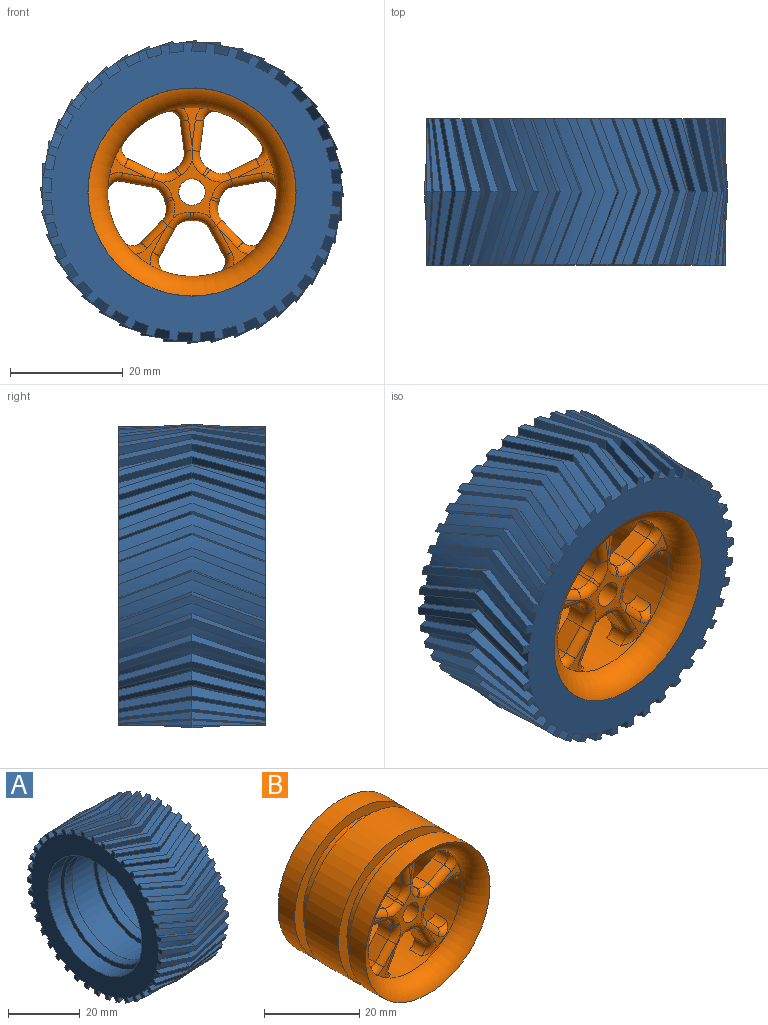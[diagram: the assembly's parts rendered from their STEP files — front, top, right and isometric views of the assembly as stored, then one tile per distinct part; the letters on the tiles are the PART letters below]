
ASSEMBLY  parts=2 mates=1
PART A: 251 faces, bbox 26x53.9x53.9 mm
  f0: cylinder r=25mm len=26mm, axis (-1,0,0), area 62.9mm2, adj f49,f50,f243,f244,f246,f247
  f1: cylinder r=25mm len=26mm, axis (-1,0,0), area 62.9mm2, adj f49,f50,f51,f52,f248,f249
  f2: cylinder r=25mm len=26mm, axis (-1,0,0), area 62.9mm2, adj f49,f50,f238,f239,f241,f242
  f3: cylinder r=25mm len=26mm, axis (-1,0,0), area 62.9mm2, adj f49,f50,f233,f234,f236,f237
  f4: cylinder r=25mm len=26mm, axis (-1,0,0), area 62.9mm2, adj f49,f50,f228,f229,f231,f232
  f5: cylinder r=25mm len=26mm, axis (-1,0,0), area 62.9mm2, adj f49,f50,f223,f224,f226,f227
  f6: cylinder r=25mm len=26mm, axis (-1,0,0), area 62.9mm2, adj f49,f50,f218,f219,f221,f222
  f7: cylinder r=25mm len=26mm, axis (-1,0,0), area 62.9mm2, adj f49,f50,f213,f214,f216,f217
  f8: cylinder r=25mm len=26mm, axis (-1,0,0), area 62.9mm2, adj f49,f50,f208,f209,f211,f212
  f9: cylinder r=25mm len=26mm, axis (-1,0,0), area 62.9mm2, adj f49,f50,f203,f204,f206,f207
  f10: cylinder r=25mm len=26mm, axis (-1,0,0), area 62.9mm2, adj f49,f50,f198,f199,f201,f202
  f11: cylinder r=25mm len=26mm, axis (-1,0,0), area 62.9mm2, adj f49,f50,f193,f194,f196,f197
  f12: cylinder r=25mm len=26mm, axis (-1,0,0), area 62.9mm2, adj f49,f50,f188,f189,f191,f192
  f13: cylinder r=25mm len=26mm, axis (-1,0,0), area 62.9mm2, adj f49,f50,f183,f184,f186,f187
  f14: cylinder r=25mm len=26mm, axis (-1,0,0), area 62.9mm2, adj f49,f50,f178,f179,f181,f182
  f15: cylinder r=25mm len=26mm, axis (-1,0,0), area 62.9mm2, adj f49,f50,f173,f174,f176,f177
  f16: cylinder r=25mm len=26mm, axis (-1,0,0), area 62.9mm2, adj f49,f50,f168,f169,f171,f172
  f17: cylinder r=25mm len=26mm, axis (-1,0,0), area 62.9mm2, adj f49,f50,f163,f164,f166,f167
  f18: cylinder r=25mm len=26mm, axis (-1,0,0), area 62.9mm2, adj f49,f50,f158,f159,f161,f162
  f19: cylinder r=25mm len=26mm, axis (-1,0,0), area 62.9mm2, adj f49,f50,f153,f154,f156,f157
  f20: cylinder r=25mm len=26mm, axis (-1,0,0), area 62.9mm2, adj f49,f50,f148,f149,f151,f152
  f21: cylinder r=25mm len=26mm, axis (-1,0,0), area 62.9mm2, adj f49,f50,f143,f144,f146,f147
  f22: cylinder r=25mm len=26mm, axis (-1,0,0), area 62.9mm2, adj f49,f50,f138,f139,f141,f142
  f23: cylinder r=25mm len=26mm, axis (-1,0,0), area 62.9mm2, adj f49,f50,f133,f134,f136,f137
  f24: cylinder r=25mm len=26mm, axis (-1,0,0), area 62.9mm2, adj f49,f50,f128,f129,f131,f132
  f25: cylinder r=25mm len=26mm, axis (-1,0,0), area 62.9mm2, adj f49,f50,f123,f124,f126,f127
  f26: cylinder r=25mm len=26mm, axis (-1,0,0), area 62.9mm2, adj f49,f50,f118,f119,f121,f122
  f27: cylinder r=25mm len=26mm, axis (-1,0,0), area 62.9mm2, adj f49,f50,f113,f114,f116,f117
  f28: cylinder r=25mm len=26mm, axis (-1,0,0), area 62.9mm2, adj f49,f50,f108,f109,f111,f112
  f29: cylinder r=25mm len=26mm, axis (-1,0,0), area 62.9mm2, adj f49,f50,f103,f104,f106,f107
  f30: cylinder r=25mm len=26mm, axis (-1,0,0), area 62.9mm2, adj f49,f50,f98,f99,f101,f102
  f31: cylinder r=25mm len=26mm, axis (-1,0,0), area 62.9mm2, adj f49,f50,f93,f94,f96,f97
  f32: cylinder r=25mm len=26mm, axis (-1,0,0), area 62.9mm2, adj f49,f50,f88,f89,f91,f92
  f33: cylinder r=25mm len=26mm, axis (-1,0,0), area 62.9mm2, adj f49,f50,f83,f84,f86,f87
  f34: cylinder r=25mm len=26mm, axis (-1,0,0), area 62.9mm2, adj f49,f50,f78,f79,f81,f82
  f35: cylinder r=25mm len=26mm, axis (-1,0,0), area 62.9mm2, adj f49,f50,f73,f74,f76,f77
  f36: cylinder r=25mm len=26mm, axis (-1,0,0), area 62.9mm2, adj f49,f50,f68,f69,f71,f72
  f37: cylinder r=25mm len=26mm, axis (-1,0,0), area 62.9mm2, adj f49,f50,f63,f64,f66,f67
  f38: cylinder r=25mm len=26mm, axis (-1,0,0), area 62.9mm2, adj f49,f50,f58,f59,f61,f62
  f39: cylinder r=25mm len=26mm, axis (-1,0,0), area 62.9mm2, adj f49,f50,f53,f54,f56,f57
  f40: cylinder r=18.5mm len=37mm, axis (-1,0,0), area 581.2mm2, adj f41,f50
  f41: plane 37x37mm, normal (-1,0,0), area 167.3mm2, adj f40,f42
  f42: cylinder r=17mm len=34mm, axis (-1,0,0), area 320.4mm2, adj f41,f43
  f43: plane 37x37mm, normal (1,0,0), area 167.3mm2, adj f42,f44
  f44: cylinder r=18.5mm len=37mm, axis (-1,0,0), area 1162.4mm2, adj f43,f45
  f45: plane 37x37mm, normal (-1,0,0), area 167.3mm2, adj f44,f46
  f46: cylinder r=17mm len=34mm, axis (-1,0,0), area 320.4mm2, adj f45,f47
  f47: plane 37x37mm, normal (1,0,0), area 167.3mm2, adj f46,f48
  f48: cylinder r=18.5mm len=37mm, axis (-1,0,0), area 581.2mm2, adj f47,f49
  f49: plane 53x53mm, normal (1,0,0), area 979.2mm2, adj f0,f1,f2,f3,f4,f5,f6,f7
  f50: plane 53x53mm, normal (-1,0,0), area 979.2mm2, adj f0,f1,f2,f3,f4,f5,f6,f7
  f51: plane 13x5.25mm, normal (-0.36,-0.92,0.15), area 23.2mm2, adj f1,f50,f52,f55
  f52: plane 13x5.25mm, normal (0.36,-0.92,0.15), area 23.2mm2, adj f1,f49,f51,f55
  f53: plane 13x5.21mm, normal (-0.36,0.92,-0.15), area 21.8mm2, adj f39,f49,f54,f55
  f54: plane 13x5.21mm, normal (0.36,0.92,-0.15), area 21.8mm2, adj f39,f50,f53,f55
  f55: plane 26x6.42mm, normal (0,0.16,0.99), area 39mm2, adj f49,f50,f51,f52,f53,f54
  f56: plane 13x5.38mm, normal (-0.36,-0.89,0.29), area 23.2mm2, adj f39,f50,f57,f60
  f57: plane 13x5.38mm, normal (0.36,-0.89,0.29), area 23.2mm2, adj f39,f49,f56,f60
  f58: plane 13x5.3mm, normal (-0.36,0.89,-0.29), area 21.8mm2, adj f38,f49,f59,f60
  f59: plane 13x5.3mm, normal (0.36,0.89,-0.29), area 21.8mm2, adj f38,f50,f58,f60
  f60: plane 26x6.18mm, normal (0,0.31,0.95), area 39mm2, adj f49,f50,f56,f57,f58,f59
  f61: plane 13x5.37mm, normal (-0.36,-0.83,0.42), area 23.2mm2, adj f38,f50,f62,f65
  f62: plane 13x5.37mm, normal (0.36,-0.83,0.42), area 23.2mm2, adj f38,f49,f61,f65
  f63: plane 13x5.25mm, normal (-0.36,0.83,-0.42), area 21.8mm2, adj f37,f49,f64,f65
  f64: plane 13x5.25mm, normal (0.36,0.83,-0.42), area 21.8mm2, adj f37,f50,f63,f65
  f65: plane 26x5.79mm, normal (0,0.45,0.89), area 39mm2, adj f49,f50,f61,f62,f63,f64
  f66: plane 13x5.22mm, normal (-0.36,-0.76,0.55), area 23.2mm2, adj f37,f50,f67,f70
  f67: plane 13x5.22mm, normal (0.36,-0.76,0.55), area 23.2mm2, adj f37,f49,f66,f70
  f68: plane 13x5.07mm, normal (-0.36,0.76,-0.55), area 21.8mm2, adj f36,f49,f69,f70
  f69: plane 13x5.07mm, normal (0.36,0.76,-0.55), area 21.8mm2, adj f36,f50,f68,f70
  f70: plane 26x5.26mm, normal (0,0.59,0.81), area 39mm2, adj f49,f50,f66,f67,f68,f69
  f71: plane 13x4.95mm, normal (-0.36,-0.66,0.66), area 23.2mm2, adj f36,f50,f72,f75
  f72: plane 13x4.95mm, normal (0.36,-0.66,0.66), area 23.2mm2, adj f36,f49,f71,f75
  f73: plane 13x4.77mm, normal (-0.36,0.66,-0.66), area 21.8mm2, adj f35,f49,f74,f75
  f74: plane 13x4.77mm, normal (0.36,0.66,-0.66), area 21.8mm2, adj f35,f50,f73,f75
  f75: plane 26x4.6mm, normal (0,0.71,0.71), area 39mm2, adj f49,f50,f71,f72,f73,f74
  f76: plane 13x4.93mm, normal (-0.36,-0.55,0.76), area 23.2mm2, adj f35,f50,f77,f80
  f77: plane 13x4.93mm, normal (0.36,-0.55,0.76), area 23.2mm2, adj f35,f49,f76,f80
  f78: plane 13x4.95mm, normal (-0.36,0.55,-0.76), area 21.8mm2, adj f34,f49,f79,f80
  f79: plane 13x4.95mm, normal (0.36,0.55,-0.76), area 21.8mm2, adj f34,f50,f78,f80
  f80: plane 26x5.26mm, normal (0,0.81,0.59), area 39mm2, adj f49,f50,f76,f77,f78,f79
  f81: plane 13x5.14mm, normal (-0.36,-0.42,0.83), area 23.2mm2, adj f34,f50,f82,f85
  f82: plane 13x5.14mm, normal (0.36,-0.42,0.83), area 23.2mm2, adj f34,f49,f81,f85
  f83: plane 13x5.16mm, normal (-0.36,0.42,-0.83), area 21.8mm2, adj f33,f49,f84,f85
  f84: plane 13x5.16mm, normal (0.36,0.42,-0.83), area 21.8mm2, adj f33,f50,f83,f85
  f85: plane 26x5.79mm, normal (0,0.89,0.45), area 39mm2, adj f49,f50,f81,f82,f83,f84
  f86: plane 13x5.22mm, normal (-0.36,-0.29,0.89), area 23.2mm2, adj f33,f50,f87,f90
  f87: plane 13x5.22mm, normal (0.36,-0.29,0.89), area 23.2mm2, adj f33,f49,f86,f90
  f88: plane 13x5.23mm, normal (-0.36,0.29,-0.89), area 21.8mm2, adj f32,f49,f89,f90
  f89: plane 13x5.23mm, normal (0.36,0.29,-0.89), area 21.8mm2, adj f32,f50,f88,f90
  f90: plane 26x6.18mm, normal (0,0.95,0.31), area 39mm2, adj f49,f50,f86,f87,f88,f89
  f91: plane 13x5.17mm, normal (-0.36,-0.15,0.92), area 23.2mm2, adj f32,f50,f92,f95
  f92: plane 13x5.17mm, normal (0.36,-0.15,0.92), area 23.2mm2, adj f32,f49,f91,f95
  f93: plane 13x5.18mm, normal (-0.36,0.15,-0.92), area 21.8mm2, adj f31,f49,f94,f95
  f94: plane 13x5.18mm, normal (0.36,0.15,-0.92), area 21.8mm2, adj f31,f50,f93,f95
  f95: plane 26x6.42mm, normal (0,0.99,0.16), area 39mm2, adj f49,f50,f91,f92,f93,f94
  f96: plane 13x5mm, normal (-0.36,0,0.93), area 23.2mm2, adj f31,f50,f97,f100
  f97: plane 13x5mm, normal (0.36,0,0.93), area 23.2mm2, adj f31,f49,f96,f100
  f98: plane 13x5mm, normal (-0.36,0,-0.93), area 21.8mm2, adj f30,f49,f99,f100
  f99: plane 13x5mm, normal (0.36,0,-0.93), area 21.8mm2, adj f30,f50,f98,f100
  f100: plane 26x6.5mm, normal (0,1,0), area 39mm2, adj f49,f50,f96,f97,f98,f99
  f101: plane 13x5.25mm, normal (-0.36,0.15,0.92), area 23.2mm2, adj f30,f50,f102,f105
  f102: plane 13x5.25mm, normal (0.36,0.15,0.92), area 23.2mm2, adj f30,f49,f101,f105
  f103: plane 13x5.21mm, normal (-0.36,-0.15,-0.92), area 21.8mm2, adj f29,f49,f104,f105
  f104: plane 13x5.21mm, normal (0.36,-0.15,-0.92), area 21.8mm2, adj f29,f50,f103,f105
  f105: plane 26x6.42mm, normal (0,0.99,-0.16), area 39mm2, adj f49,f50,f101,f102,f103,f104
  f106: plane 13x5.38mm, normal (-0.36,0.29,0.89), area 23.2mm2, adj f29,f50,f107,f110
  f107: plane 13x5.38mm, normal (0.36,0.29,0.89), area 23.2mm2, adj f29,f49,f106,f110
  f108: plane 13x5.3mm, normal (-0.36,-0.29,-0.89), area 21.8mm2, adj f28,f49,f109,f110
  f109: plane 13x5.3mm, normal (0.36,-0.29,-0.89), area 21.8mm2, adj f28,f50,f108,f110
  f110: plane 26x6.18mm, normal (0,0.95,-0.31), area 39mm2, adj f49,f50,f106,f107,f108,f109
  f111: plane 13x5.37mm, normal (-0.36,0.42,0.83), area 23.2mm2, adj f28,f50,f112,f115
  f112: plane 13x5.37mm, normal (0.36,0.42,0.83), area 23.2mm2, adj f28,f49,f111,f115
  f113: plane 13x5.25mm, normal (-0.36,-0.42,-0.83), area 21.8mm2, adj f27,f49,f114,f115
  f114: plane 13x5.25mm, normal (0.36,-0.42,-0.83), area 21.8mm2, adj f27,f50,f113,f115
  f115: plane 26x5.79mm, normal (0,0.89,-0.45), area 39mm2, adj f49,f50,f111,f112,f113,f114
  f116: plane 13x5.22mm, normal (-0.36,0.55,0.76), area 23.2mm2, adj f27,f50,f117,f120
  f117: plane 13x5.22mm, normal (0.36,0.55,0.76), area 23.2mm2, adj f27,f49,f116,f120
  f118: plane 13x5.07mm, normal (-0.36,-0.55,-0.76), area 21.8mm2, adj f26,f49,f119,f120
  f119: plane 13x5.07mm, normal (0.36,-0.55,-0.76), area 21.8mm2, adj f26,f50,f118,f120
  f120: plane 26x5.26mm, normal (0,0.81,-0.59), area 39mm2, adj f49,f50,f116,f117,f118,f119
  f121: plane 13x4.95mm, normal (-0.36,0.66,0.66), area 23.2mm2, adj f26,f50,f122,f125
  f122: plane 13x4.95mm, normal (0.36,0.66,0.66), area 23.2mm2, adj f26,f49,f121,f125
  f123: plane 13x4.77mm, normal (-0.36,-0.66,-0.66), area 21.8mm2, adj f25,f49,f124,f125
  f124: plane 13x4.77mm, normal (0.36,-0.66,-0.66), area 21.8mm2, adj f25,f50,f123,f125
  f125: plane 26x4.6mm, normal (0,0.71,-0.71), area 39mm2, adj f49,f50,f121,f122,f123,f124
  f126: plane 13x4.93mm, normal (-0.36,0.76,0.55), area 23.2mm2, adj f25,f50,f127,f130
  f127: plane 13x4.93mm, normal (0.36,0.76,0.55), area 23.2mm2, adj f25,f49,f126,f130
  f128: plane 13x4.95mm, normal (-0.36,-0.76,-0.55), area 21.8mm2, adj f24,f49,f129,f130
  f129: plane 13x4.95mm, normal (0.36,-0.76,-0.55), area 21.8mm2, adj f24,f50,f128,f130
  f130: plane 26x5.26mm, normal (0,0.59,-0.81), area 39mm2, adj f49,f50,f126,f127,f128,f129
  f131: plane 13x5.14mm, normal (-0.36,0.83,0.42), area 23.2mm2, adj f24,f50,f132,f135
  f132: plane 13x5.14mm, normal (0.36,0.83,0.42), area 23.2mm2, adj f24,f49,f131,f135
  f133: plane 13x5.16mm, normal (-0.36,-0.83,-0.42), area 21.8mm2, adj f23,f49,f134,f135
  f134: plane 13x5.16mm, normal (0.36,-0.83,-0.42), area 21.8mm2, adj f23,f50,f133,f135
  f135: plane 26x5.79mm, normal (0,0.45,-0.89), area 39mm2, adj f49,f50,f131,f132,f133,f134
  f136: plane 13x5.22mm, normal (-0.36,0.89,0.29), area 23.2mm2, adj f23,f50,f137,f140
  f137: plane 13x5.22mm, normal (0.36,0.89,0.29), area 23.2mm2, adj f23,f49,f136,f140
  f138: plane 13x5.23mm, normal (-0.36,-0.89,-0.29), area 21.8mm2, adj f22,f49,f139,f140
  f139: plane 13x5.23mm, normal (0.36,-0.89,-0.29), area 21.8mm2, adj f22,f50,f138,f140
  f140: plane 26x6.18mm, normal (0,0.31,-0.95), area 39mm2, adj f49,f50,f136,f137,f138,f139
  f141: plane 13x5.17mm, normal (-0.36,0.92,0.15), area 23.2mm2, adj f22,f50,f142,f145
  f142: plane 13x5.17mm, normal (0.36,0.92,0.15), area 23.2mm2, adj f22,f49,f141,f145
  f143: plane 13x5.18mm, normal (-0.36,-0.92,-0.15), area 21.8mm2, adj f21,f49,f144,f145
  f144: plane 13x5.18mm, normal (0.36,-0.92,-0.15), area 21.8mm2, adj f21,f50,f143,f145
  f145: plane 26x6.42mm, normal (0,0.16,-0.99), area 39mm2, adj f49,f50,f141,f142,f143,f144
  f146: plane 13x5mm, normal (-0.36,0.93,0), area 23.2mm2, adj f21,f50,f147,f150
  f147: plane 13x5mm, normal (0.36,0.93,0), area 23.2mm2, adj f21,f49,f146,f150
  f148: plane 13x5mm, normal (-0.36,-0.93,0), area 21.8mm2, adj f20,f49,f149,f150
  f149: plane 13x5mm, normal (0.36,-0.93,0), area 21.8mm2, adj f20,f50,f148,f150
  f150: plane 26x6.5mm, normal (0,0,-1), area 39mm2, adj f49,f50,f146,f147,f148,f149
  f151: plane 13x5.25mm, normal (-0.36,0.92,-0.15), area 23.2mm2, adj f20,f50,f152,f155
  f152: plane 13x5.25mm, normal (0.36,0.92,-0.15), area 23.2mm2, adj f20,f49,f151,f155
  f153: plane 13x5.21mm, normal (-0.36,-0.92,0.15), area 21.8mm2, adj f19,f49,f154,f155
  f154: plane 13x5.21mm, normal (0.36,-0.92,0.15), area 21.8mm2, adj f19,f50,f153,f155
  f155: plane 26x6.42mm, normal (0,-0.16,-0.99), area 39mm2, adj f49,f50,f151,f152,f153,f154
  f156: plane 13x5.38mm, normal (-0.36,0.89,-0.29), area 23.2mm2, adj f19,f50,f157,f160
  f157: plane 13x5.38mm, normal (0.36,0.89,-0.29), area 23.2mm2, adj f19,f49,f156,f160
  f158: plane 13x5.3mm, normal (-0.36,-0.89,0.29), area 21.8mm2, adj f18,f49,f159,f160
  f159: plane 13x5.3mm, normal (0.36,-0.89,0.29), area 21.8mm2, adj f18,f50,f158,f160
  f160: plane 26x6.18mm, normal (0,-0.31,-0.95), area 39mm2, adj f49,f50,f156,f157,f158,f159
  f161: plane 13x5.37mm, normal (-0.36,0.83,-0.42), area 23.2mm2, adj f18,f50,f162,f165
  f162: plane 13x5.37mm, normal (0.36,0.83,-0.42), area 23.2mm2, adj f18,f49,f161,f165
  f163: plane 13x5.25mm, normal (-0.36,-0.83,0.42), area 21.8mm2, adj f17,f49,f164,f165
  f164: plane 13x5.25mm, normal (0.36,-0.83,0.42), area 21.8mm2, adj f17,f50,f163,f165
  f165: plane 26x5.79mm, normal (0,-0.45,-0.89), area 39mm2, adj f49,f50,f161,f162,f163,f164
  f166: plane 13x5.22mm, normal (-0.36,0.76,-0.55), area 23.2mm2, adj f17,f50,f167,f170
  f167: plane 13x5.22mm, normal (0.36,0.76,-0.55), area 23.2mm2, adj f17,f49,f166,f170
  f168: plane 13x5.07mm, normal (-0.36,-0.76,0.55), area 21.8mm2, adj f16,f49,f169,f170
  f169: plane 13x5.07mm, normal (0.36,-0.76,0.55), area 21.8mm2, adj f16,f50,f168,f170
  f170: plane 26x5.26mm, normal (0,-0.59,-0.81), area 39mm2, adj f49,f50,f166,f167,f168,f169
  f171: plane 13x4.95mm, normal (-0.36,0.66,-0.66), area 23.2mm2, adj f16,f50,f172,f175
  f172: plane 13x4.95mm, normal (0.36,0.66,-0.66), area 23.2mm2, adj f16,f49,f171,f175
  f173: plane 13x4.77mm, normal (-0.36,-0.66,0.66), area 21.8mm2, adj f15,f49,f174,f175
  f174: plane 13x4.77mm, normal (0.36,-0.66,0.66), area 21.8mm2, adj f15,f50,f173,f175
  f175: plane 26x4.6mm, normal (0,-0.71,-0.71), area 39mm2, adj f49,f50,f171,f172,f173,f174
  f176: plane 13x4.93mm, normal (-0.36,0.55,-0.76), area 23.2mm2, adj f15,f50,f177,f180
  f177: plane 13x4.93mm, normal (0.36,0.55,-0.76), area 23.2mm2, adj f15,f49,f176,f180
  f178: plane 13x4.95mm, normal (-0.36,-0.55,0.76), area 21.8mm2, adj f14,f49,f179,f180
  f179: plane 13x4.95mm, normal (0.36,-0.55,0.76), area 21.8mm2, adj f14,f50,f178,f180
  f180: plane 26x5.26mm, normal (0,-0.81,-0.59), area 39mm2, adj f49,f50,f176,f177,f178,f179
  f181: plane 13x5.14mm, normal (-0.36,0.42,-0.83), area 23.2mm2, adj f14,f50,f182,f185
  f182: plane 13x5.14mm, normal (0.36,0.42,-0.83), area 23.2mm2, adj f14,f49,f181,f185
  f183: plane 13x5.16mm, normal (-0.36,-0.42,0.83), area 21.8mm2, adj f13,f49,f184,f185
  f184: plane 13x5.16mm, normal (0.36,-0.42,0.83), area 21.8mm2, adj f13,f50,f183,f185
  f185: plane 26x5.79mm, normal (0,-0.89,-0.45), area 39mm2, adj f49,f50,f181,f182,f183,f184
  f186: plane 13x5.22mm, normal (-0.36,0.29,-0.89), area 23.2mm2, adj f13,f50,f187,f190
  f187: plane 13x5.22mm, normal (0.36,0.29,-0.89), area 23.2mm2, adj f13,f49,f186,f190
  f188: plane 13x5.23mm, normal (-0.36,-0.29,0.89), area 21.8mm2, adj f12,f49,f189,f190
  f189: plane 13x5.23mm, normal (0.36,-0.29,0.89), area 21.8mm2, adj f12,f50,f188,f190
  f190: plane 26x6.18mm, normal (0,-0.95,-0.31), area 39mm2, adj f49,f50,f186,f187,f188,f189
  f191: plane 13x5.17mm, normal (-0.36,0.15,-0.92), area 23.2mm2, adj f12,f50,f192,f195
  f192: plane 13x5.17mm, normal (0.36,0.15,-0.92), area 23.2mm2, adj f12,f49,f191,f195
  f193: plane 13x5.18mm, normal (-0.36,-0.15,0.92), area 21.8mm2, adj f11,f49,f194,f195
  f194: plane 13x5.18mm, normal (0.36,-0.15,0.92), area 21.8mm2, adj f11,f50,f193,f195
  f195: plane 26x6.42mm, normal (0,-0.99,-0.16), area 39mm2, adj f49,f50,f191,f192,f193,f194
  f196: plane 13x5mm, normal (-0.36,0,-0.93), area 23.2mm2, adj f11,f50,f197,f200
  f197: plane 13x5mm, normal (0.36,0,-0.93), area 23.2mm2, adj f11,f49,f196,f200
  f198: plane 13x5mm, normal (-0.36,0,0.93), area 21.8mm2, adj f10,f49,f199,f200
  f199: plane 13x5mm, normal (0.36,0,0.93), area 21.8mm2, adj f10,f50,f198,f200
  f200: plane 26x6.5mm, normal (0,-1,0), area 39mm2, adj f49,f50,f196,f197,f198,f199
  f201: plane 13x5.25mm, normal (-0.36,-0.15,-0.92), area 23.2mm2, adj f10,f50,f202,f205
  f202: plane 13x5.25mm, normal (0.36,-0.15,-0.92), area 23.2mm2, adj f10,f49,f201,f205
  f203: plane 13x5.21mm, normal (-0.36,0.15,0.92), area 21.8mm2, adj f9,f49,f204,f205
  f204: plane 13x5.21mm, normal (0.36,0.15,0.92), area 21.8mm2, adj f9,f50,f203,f205
  f205: plane 26x6.42mm, normal (0,-0.99,0.16), area 39mm2, adj f49,f50,f201,f202,f203,f204
  f206: plane 13x5.38mm, normal (-0.36,-0.29,-0.89), area 23.2mm2, adj f9,f50,f207,f210
  f207: plane 13x5.38mm, normal (0.36,-0.29,-0.89), area 23.2mm2, adj f9,f49,f206,f210
  f208: plane 13x5.3mm, normal (-0.36,0.29,0.89), area 21.8mm2, adj f8,f49,f209,f210
  f209: plane 13x5.3mm, normal (0.36,0.29,0.89), area 21.8mm2, adj f8,f50,f208,f210
  f210: plane 26x6.18mm, normal (0,-0.95,0.31), area 39mm2, adj f49,f50,f206,f207,f208,f209
  f211: plane 13x5.37mm, normal (-0.36,-0.42,-0.83), area 23.2mm2, adj f8,f50,f212,f215
  f212: plane 13x5.37mm, normal (0.36,-0.42,-0.83), area 23.2mm2, adj f8,f49,f211,f215
  f213: plane 13x5.25mm, normal (-0.36,0.42,0.83), area 21.8mm2, adj f7,f49,f214,f215
  f214: plane 13x5.25mm, normal (0.36,0.42,0.83), area 21.8mm2, adj f7,f50,f213,f215
  f215: plane 26x5.79mm, normal (0,-0.89,0.45), area 39mm2, adj f49,f50,f211,f212,f213,f214
  f216: plane 13x5.22mm, normal (-0.36,-0.55,-0.76), area 23.2mm2, adj f7,f50,f217,f220
  f217: plane 13x5.22mm, normal (0.36,-0.55,-0.76), area 23.2mm2, adj f7,f49,f216,f220
  f218: plane 13x5.07mm, normal (-0.36,0.55,0.76), area 21.8mm2, adj f6,f49,f219,f220
  f219: plane 13x5.07mm, normal (0.36,0.55,0.76), area 21.8mm2, adj f6,f50,f218,f220
  f220: plane 26x5.26mm, normal (0,-0.81,0.59), area 39mm2, adj f49,f50,f216,f217,f218,f219
  f221: plane 13x4.95mm, normal (-0.36,-0.66,-0.66), area 23.2mm2, adj f6,f50,f222,f225
  f222: plane 13x4.95mm, normal (0.36,-0.66,-0.66), area 23.2mm2, adj f6,f49,f221,f225
  f223: plane 13x4.77mm, normal (-0.36,0.66,0.66), area 21.8mm2, adj f5,f49,f224,f225
  f224: plane 13x4.77mm, normal (0.36,0.66,0.66), area 21.8mm2, adj f5,f50,f223,f225
  f225: plane 26x4.6mm, normal (0,-0.71,0.71), area 39mm2, adj f49,f50,f221,f222,f223,f224
  f226: plane 13x4.93mm, normal (-0.36,-0.76,-0.55), area 23.2mm2, adj f5,f50,f227,f230
  f227: plane 13x4.93mm, normal (0.36,-0.76,-0.55), area 23.2mm2, adj f5,f49,f226,f230
  f228: plane 13x4.95mm, normal (-0.36,0.76,0.55), area 21.8mm2, adj f4,f49,f229,f230
  f229: plane 13x4.95mm, normal (0.36,0.76,0.55), area 21.8mm2, adj f4,f50,f228,f230
  f230: plane 26x5.26mm, normal (0,-0.59,0.81), area 39mm2, adj f49,f50,f226,f227,f228,f229
  f231: plane 13x5.14mm, normal (-0.36,-0.83,-0.42), area 23.2mm2, adj f4,f50,f232,f235
  f232: plane 13x5.14mm, normal (0.36,-0.83,-0.42), area 23.2mm2, adj f4,f49,f231,f235
  f233: plane 13x5.16mm, normal (-0.36,0.83,0.42), area 21.8mm2, adj f3,f49,f234,f235
  f234: plane 13x5.16mm, normal (0.36,0.83,0.42), area 21.8mm2, adj f3,f50,f233,f235
  f235: plane 26x5.79mm, normal (0,-0.45,0.89), area 39mm2, adj f49,f50,f231,f232,f233,f234
  f236: plane 13x5.22mm, normal (-0.36,-0.89,-0.29), area 23.2mm2, adj f3,f50,f237,f240
  f237: plane 13x5.22mm, normal (0.36,-0.89,-0.29), area 23.2mm2, adj f3,f49,f236,f240
  f238: plane 13x5.23mm, normal (-0.36,0.89,0.29), area 21.8mm2, adj f2,f49,f239,f240
  f239: plane 13x5.23mm, normal (0.36,0.89,0.29), area 21.8mm2, adj f2,f50,f238,f240
  f240: plane 26x6.18mm, normal (0,-0.31,0.95), area 39mm2, adj f49,f50,f236,f237,f238,f239
  f241: plane 13x5.17mm, normal (-0.36,-0.92,-0.15), area 23.2mm2, adj f2,f50,f242,f245
  f242: plane 13x5.17mm, normal (0.36,-0.92,-0.15), area 23.2mm2, adj f2,f49,f241,f245
  f243: plane 13x5.18mm, normal (-0.36,0.92,0.15), area 21.8mm2, adj f0,f49,f244,f245
  f244: plane 13x5.18mm, normal (0.36,0.92,0.15), area 21.8mm2, adj f0,f50,f243,f245
  f245: plane 26x6.42mm, normal (0,-0.16,0.99), area 39mm2, adj f49,f50,f241,f242,f243,f244
  f246: plane 13x5mm, normal (-0.36,-0.93,0), area 23.2mm2, adj f0,f50,f247,f250
  f247: plane 13x5mm, normal (0.36,-0.93,0), area 23.2mm2, adj f0,f49,f246,f250
  f248: plane 13x5mm, normal (-0.36,0.93,0), area 21.8mm2, adj f1,f49,f249,f250
  f249: plane 13x5mm, normal (0.36,0.93,0), area 21.8mm2, adj f1,f50,f248,f250
  f250: plane 26x6.5mm, normal (0,0,1), area 39mm2, adj f49,f50,f246,f247,f248,f249
PART B: 98 faces, bbox 43.3x26.2x43.3 mm
  f0: cylinder r=2.35mm len=16mm, axis (0,-1,0), area 236.4mm2, adj f2,f91
  f1: plane 10.2x10.2mm, normal (0,1,0), area 47.4mm2, adj f19,f92,f93,f94,f95,f96,f97
  f2: plane 10.85x10.32mm, normal (0,-1,0), area 34.9mm2, adj f0,f61,f62,f66,f67,f71,f72,f75
  f3: plane 6.88x3.66mm, normal (0,-1,0), area 7.1mm2, adj f17,f77,f82,f83,f87
  f4: plane 6.78x3.36mm, normal (0,-1,0), area 7.1mm2, adj f17,f74,f78,f79,f84
  f5: plane 6.88x3.66mm, normal (0,-1,0), area 7.1mm2, adj f17,f60,f64,f65,f70
  f6: plane 6.4x5.29mm, normal (0,-1,0), area 7.1mm2, adj f17,f56,f57,f58,f59
  f7: cylinder r=18.5mm len=37mm, axis (0,-1,0), area 581.2mm2, adj f8,f18
  f8: plane 37x37mm, normal (0,1,0), area 271mm2, adj f7,f9
  f9: cylinder r=16mm len=32mm, axis (0,-1,0), area 301.6mm2, adj f8,f12
  f10: cylinder r=18.5mm len=37mm, axis (0,-1,0), area 1162.4mm2, adj f11,f12
  f11: plane 37x37mm, normal (0,1,0), area 271mm2, adj f10,f13
  f12: plane 37x37mm, normal (0,-1,0), area 271mm2, adj f9,f10
  f13: cylinder r=16mm len=32mm, axis (0,-1,0), area 301.6mm2, adj f11,f16
  f14: cylinder r=18.5mm len=37mm, axis (0,-1,0), area 581.2mm2, adj f15,f16
  f15: plane 37x37mm, normal (0,1,0), area 368.4mm2, adj f14,f17
  f16: plane 37x37mm, normal (0,-1,0), area 271mm2, adj f13,f14
  f17: cylinder r=15mm len=30mm, axis (0,-1,0), area 1778.6mm2, adj f3,f4,f5,f6,f15,f18,f20,f23
  f18: torus R=20mm, axis (0,-1,0), area 645.7mm2, adj f7,f17
  f19: cylinder r=5.1mm len=19.5mm, axis (0,-1,0), area 523.6mm2, adj f1,f23,f26,f29,f32,f35,f46,f47
  f20: plane 6.4x5.29mm, normal (0,-1,0), area 7.1mm2, adj f17,f63,f68,f69,f73
  f21: plane 5.39x3.5mm, normal (0.99,0,-0.13), area 19mm2, adj f23,f42,f52,f79
  f22: plane 5.39x3.5mm, normal (-0.99,0,-0.13), area 19mm2, adj f23,f43,f53,f84
  f23: plane 10.7x9.39mm, normal (0,1,0), area 38.4mm2, adj f17,f19,f21,f22,f42,f43,f52,f53
  f24: plane 4.91x3.5mm, normal (-0.43,0,0.9), area 19mm2, adj f26,f41,f51,f70
  f25: plane 5.34x3.5mm, normal (0.18,0,-0.98), area 19mm2, adj f26,f40,f50,f65
  f26: plane 11.76x10.15mm, normal (0,1,0), area 38.4mm2, adj f17,f19,f24,f25,f40,f41,f50,f51
  f27: plane 5.34x3.5mm, normal (-0.18,0,-0.98), area 19mm2, adj f29,f45,f55,f82
  f28: plane 4.91x3.5mm, normal (0.43,0,0.9), area 19mm2, adj f29,f44,f54,f87
  f29: plane 11.76x10.15mm, normal (0,1,0), area 38.4mm2, adj f17,f19,f27,f28,f44,f45,f54,f55
  f30: plane 4.77x3.5mm, normal (0.88,0,-0.48), area 19mm2, adj f32,f37,f47,f68
  f31: plane 3.95x3.74mm, normal (-0.73,0,0.69), area 19mm2, adj f32,f36,f46,f73
  f32: plane 12.42x11.86mm, normal (0,1,0), area 38.4mm2, adj f17,f19,f30,f31,f36,f37,f46,f47
  f33: plane 3.95x3.74mm, normal (0.73,0,0.69), area 19mm2, adj f35,f39,f49,f58
  f34: plane 4.77x3.5mm, normal (-0.88,0,-0.48), area 19mm2, adj f35,f38,f48,f59
  f35: plane 12.42x11.86mm, normal (0,1,0), area 38.4mm2, adj f17,f19,f33,f34,f38,f39,f48,f49
  f36: cylinder r=2mm len=3.5mm, axis (0,-1,0), area 12.3mm2, adj f17,f31,f32,f69
  f37: cylinder r=2mm len=3.5mm, axis (0,-1,0), area 12.3mm2, adj f17,f30,f32,f63
  f38: cylinder r=2mm len=3.5mm, axis (0,-1,0), area 12.3mm2, adj f17,f34,f35,f57
  f39: cylinder r=2mm len=3.5mm, axis (0,-1,0), area 12.3mm2, adj f17,f33,f35,f56
  f40: cylinder r=2mm len=3.5mm, axis (0,-1,0), area 12.3mm2, adj f17,f25,f26,f60
  f41: cylinder r=2mm len=3.5mm, axis (0,-1,0), area 12.3mm2, adj f17,f24,f26,f64
  f42: cylinder r=2mm len=3.5mm, axis (0,-1,0), area 12.3mm2, adj f17,f21,f23,f74
  f43: cylinder r=2mm len=3.5mm, axis (0,-1,0), area 12.3mm2, adj f17,f22,f23,f78
  f44: cylinder r=2mm len=3.5mm, axis (0,-1,0), area 12.3mm2, adj f17,f28,f29,f83
  f45: cylinder r=2mm len=3.5mm, axis (0,-1,0), area 12.3mm2, adj f17,f27,f29,f77
  f46: cylinder r=3mm len=3.5mm, axis (0,-1,0), area 11.9mm2, adj f19,f31,f32,f76
  f47: cylinder r=3mm len=3.5mm, axis (0,-1,0), area 11.9mm2, adj f19,f30,f32,f72
  f48: cylinder r=3mm len=3.5mm, axis (0,-1,0), area 11.9mm2, adj f19,f34,f35,f62
  f49: cylinder r=3mm len=3.5mm, axis (0,-1,0), area 11.9mm2, adj f19,f33,f35,f61
  f50: cylinder r=3mm len=3.5mm, axis (0,-1,0), area 11.9mm2, adj f19,f25,f26,f71
  f51: cylinder r=3mm len=3.5mm, axis (0,-1,0), area 11.9mm2, adj f19,f24,f26,f75
  f52: cylinder r=3mm len=3.5mm, axis (0,-1,0), area 11.9mm2, adj f19,f21,f23,f85
  f53: cylinder r=3mm len=3.5mm, axis (0,-1,0), area 11.9mm2, adj f19,f22,f23,f88
  f54: cylinder r=3mm len=3.5mm, axis (0,-1,0), area 11.9mm2, adj f19,f28,f29,f89
  f55: cylinder r=3mm len=3.5mm, axis (0,-1,0), area 11.9mm2, adj f19,f27,f29,f86
  f56: torus R=3.5mm, axis (0,-1,0), area 6.5mm2, adj f6,f17,f39,f58
  f57: torus R=3.5mm, axis (0,-1,0), area 6.5mm2, adj f6,f17,f38,f59
  f58: cylinder r=1.5mm len=4.98mm, axis (-0.69,0,0.73), area 12.8mm2, adj f6,f33,f56,f59,f61
  f59: cylinder r=1.5mm len=5.49mm, axis (0.48,0,-0.88), area 12.8mm2, adj f6,f34,f57,f58,f62
  f60: torus R=3.5mm, axis (0,-1,0), area 6.5mm2, adj f5,f17,f40,f65
  f61: torus R=4.5mm, axis (0,-1,0), area 9.3mm2, adj f2,f49,f58,f62,f66
  f62: torus R=4.5mm, axis (0,-1,0), area 9.3mm2, adj f2,f48,f59,f61,f67
  f63: torus R=3.5mm, axis (0,-1,0), area 6.5mm2, adj f17,f20,f37,f68
  f64: torus R=3.5mm, axis (0,-1,0), area 6.5mm2, adj f5,f17,f41,f70
  f65: cylinder r=1.5mm len=5.62mm, axis (0.98,0,0.18), area 12.8mm2, adj f5,f25,f60,f70,f71
  f66: torus R=3.6mm, axis (0,-1,0), area 1.3mm2, adj f2,f19,f61,f71
  f67: torus R=3.6mm, axis (0,-1,0), area 1.3mm2, adj f2,f19,f62,f72
  f68: cylinder r=1.5mm len=5.49mm, axis (0.48,0,0.88), area 12.8mm2, adj f20,f30,f63,f72,f73
  f69: torus R=3.5mm, axis (0,-1,0), area 6.5mm2, adj f17,f20,f36,f73
  f70: cylinder r=1.5mm len=5.55mm, axis (-0.9,0,-0.43), area 12.8mm2, adj f5,f24,f64,f65,f75
  f71: torus R=4.5mm, axis (0,-1,0), area 9.3mm2, adj f2,f50,f65,f66,f75
  f72: torus R=4.5mm, axis (0,-1,0), area 9.3mm2, adj f2,f47,f67,f68,f76
  f73: cylinder r=1.5mm len=4.98mm, axis (-0.69,0,-0.73), area 12.8mm2, adj f20,f31,f68,f69,f76
  f74: torus R=3.5mm, axis (0,-1,0), area 6.5mm2, adj f4,f17,f42,f79
  f75: torus R=4.5mm, axis (0,-1,0), area 9.3mm2, adj f2,f51,f70,f71,f80
  f76: torus R=4.5mm, axis (0,-1,0), area 9.3mm2, adj f2,f46,f72,f73,f81
  f77: torus R=3.5mm, axis (0,-1,0), area 6.5mm2, adj f3,f17,f45,f82
  f78: torus R=3.5mm, axis (0,-1,0), area 6.5mm2, adj f4,f17,f43,f84
  f79: cylinder r=1.5mm len=5.58mm, axis (0.13,0,0.99), area 12.8mm2, adj f4,f21,f74,f84,f85
  f80: torus R=3.6mm, axis (0,-1,0), area 1.3mm2, adj f2,f19,f75,f85
  f81: torus R=3.6mm, axis (0,-1,0), area 1.3mm2, adj f2,f19,f76,f86
  f82: cylinder r=1.5mm len=5.62mm, axis (0.98,0,-0.18), area 12.8mm2, adj f3,f27,f77,f86,f87
  f83: torus R=3.5mm, axis (0,-1,0), area 6.5mm2, adj f3,f17,f44,f87
  f84: cylinder r=1.5mm len=5.58mm, axis (0.13,0,-0.99), area 12.8mm2, adj f4,f22,f78,f79,f88
  f85: torus R=4.5mm, axis (0,-1,0), area 9.3mm2, adj f2,f52,f79,f80,f88
  f86: torus R=4.5mm, axis (0,-1,0), area 9.3mm2, adj f2,f55,f81,f82,f89
  f87: cylinder r=1.5mm len=5.55mm, axis (-0.9,0,0.43), area 12.8mm2, adj f3,f28,f82,f83,f89
  f88: torus R=4.5mm, axis (0,-1,0), area 9.3mm2, adj f2,f53,f84,f85,f90
  f89: torus R=4.5mm, axis (0,-1,0), area 9.3mm2, adj f2,f54,f86,f87,f90
  f90: torus R=3.6mm, axis (0,-1,0), area 1.3mm2, adj f2,f19,f88,f89
  f91: plane 7.19x6.77mm, normal (0,1,0), area 17mm2, adj f0,f92,f93,f94,f95,f96,f97
  f92: plane 5x2.84mm, normal (0.62,0,0.78), area 18.2mm2, adj f1,f91,f93,f97
  f93: plane 5x3.6mm, normal (0.99,0,-0.15), area 18.2mm2, adj f1,f91,f92,f94
  f94: plane 5x3.39mm, normal (0.36,0,-0.93), area 18.2mm2, adj f1,f91,f93,f95
  f95: plane 5x2.84mm, normal (-0.62,0,-0.78), area 18.2mm2, adj f1,f91,f94,f96
  f96: plane 5x3.6mm, normal (-0.99,0,0.15), area 18.2mm2, adj f1,f91,f95,f97
  f97: plane 5x3.39mm, normal (-0.36,0,0.93), area 18.2mm2, adj f1,f91,f92,f96
PLACE A rot(axis=(-0.58,-0.58,0.58),120deg) t=(-1.59,6.02,7.41)mm fixed
PLACE B t=(-1.59,-6.98,7.41)mm
MATE fastened B.f0 <-> A.f0  axis (0,-1,0) through (-1.59,-6.98,7.41)mm
